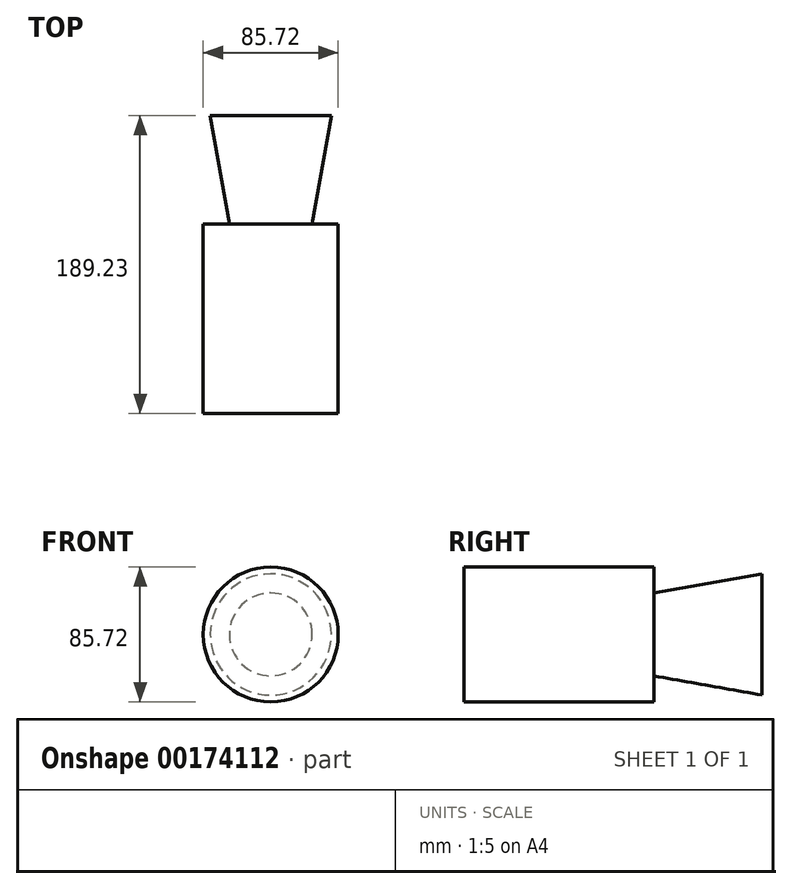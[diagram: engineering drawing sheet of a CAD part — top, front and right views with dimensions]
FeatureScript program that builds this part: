
annotation { "Feature Type Name" : "Feature", "Feature Type Description" : "" }
export const myFeature = defineFeature(function(context is Context, id is Id, definition is map)
    precondition{}
    {
        {
            var Q0;
            Q0=qCreatedBy(makeId("Front.planeOp"),FACE);
            var sketch = newSketch(context, id + "F0", { "sketchPlane" : qUnion([Q0])});
            skCircle(sketch, "E0", {"center": v(0, 0) * mm, "radius": 42.86 * mm});
            skSolve(sketch);
        }
        {
            var Q0;
            Q0 = qSketchRegion(id + "F0", true);
            extrude(context, id + "F1", {"entities" : qUnion([Q0]), "depth" : 120.4 * mm});
        }
        {
            var Q0;
            Q0=qCreatedBy(makeId("Front.planeOp"),FACE);
            var sketch = newSketch(context, id + "F2", { "sketchPlane" : qUnion([Q0])});
            skCircle(sketch, "E1", {"center": v(0, 0) * mm, "radius": 26.3 * mm});
            skSolve(sketch);
        }
        {
            var Q0;
            Q0=makeQuery(id+"F2.imprint","IMPRINT",FACE,{"disambiguationData":[TD([[makeQuery(id+"F2.imprint","IMPRINT",EDGE,{"derivedFrom":sQuery(id+"F2.wireOp",EDGE,"E1")}),1.0]])]});
            extrude(context, id + "F3", {"entities" : qUnion([Q0]), "operationType" : NewBodyOperationType.ADD, "oppositeDirection" : true, "depth" : 68.83 * mm, "hasDraft" : true, "draftAngle" : 10 * degree});
        }
    });
